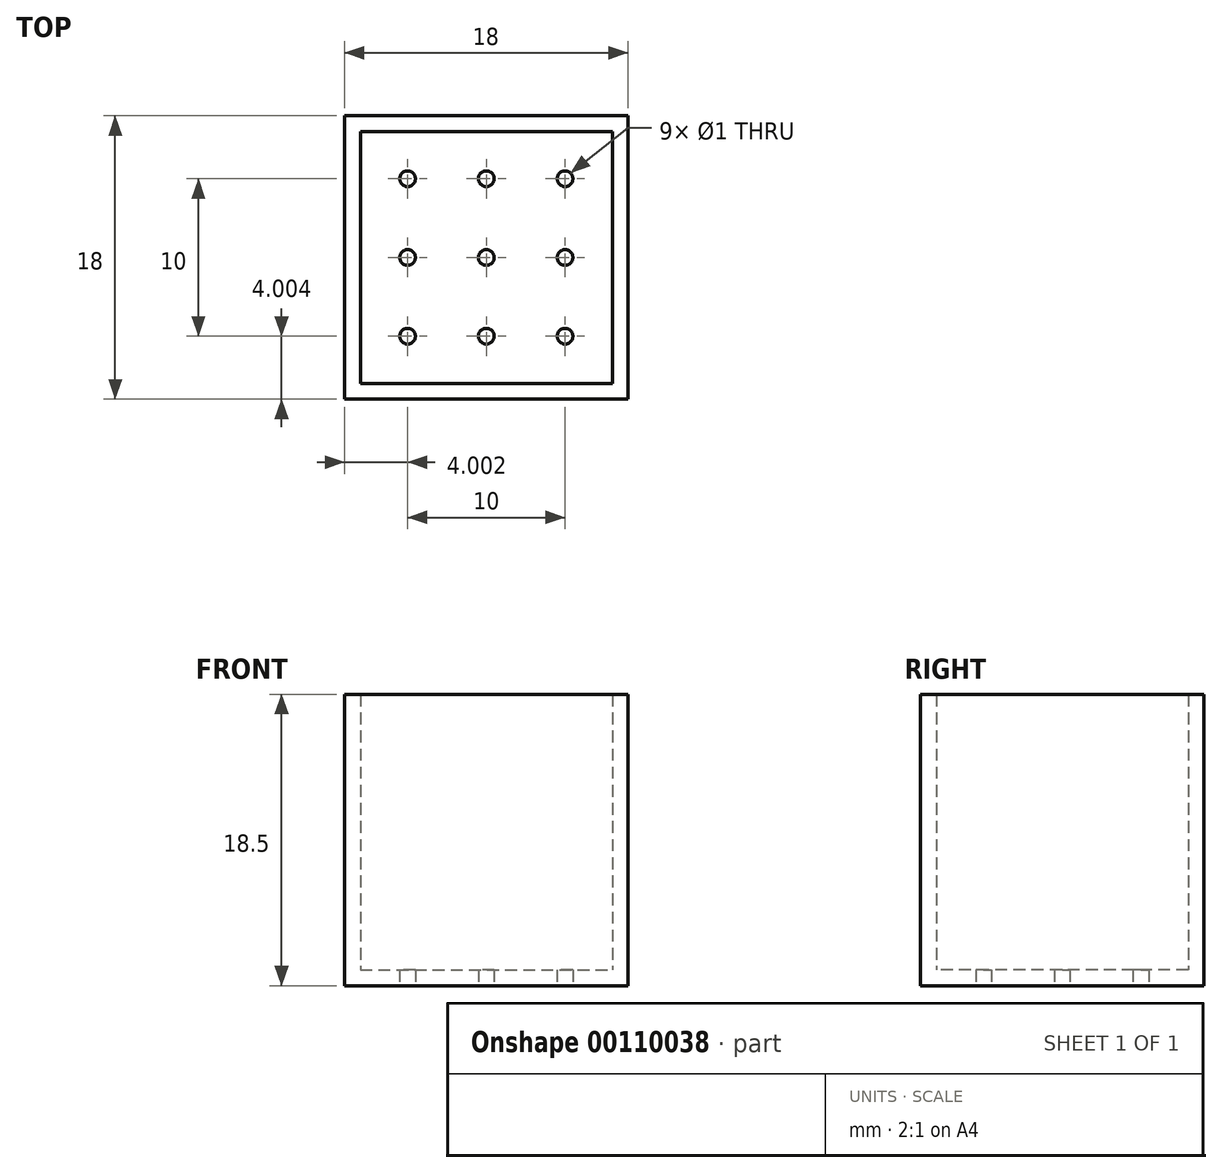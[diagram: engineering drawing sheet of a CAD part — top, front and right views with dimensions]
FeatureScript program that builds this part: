
annotation { "Feature Type Name" : "Feature", "Feature Type Description" : "" }
export const myFeature = defineFeature(function(context is Context, id is Id, definition is map)
    precondition{}
    {
        {
            var Q0;
            Q0=qCreatedBy(makeId("Top.planeOp"),FACE);
            var sketch = newSketch(context, id + "F0", { "sketchPlane" : qUnion([Q0])});
            skLineSegment(sketch, "E0.bottom", {"start": v(-1.53, -8.57) * mm, "end": v(16.47, -8.57) * mm});
            skLineSegment(sketch, "E0.top", {"start": v(-1.53, -26.57) * mm, "end": v(16.47, -26.57) * mm});
            skLineSegment(sketch, "E0.left", {"start": v(-1.53, -8.57) * mm, "end": v(-1.53, -26.57) * mm});
            skLineSegment(sketch, "E0.right", {"start": v(16.47, -8.57) * mm, "end": v(16.47, -26.57) * mm});
            skSolve(sketch);
        }
        {
            var Q0;
            Q0=qSketchRegion(id+"F0",true);
            extrude(context, id + "F1", {"entities" : qUnion([Q0]), "depth" : 18.5 * mm});
        }
        {
            var Q0;
            Q0=makeQuery(id+"F1.opExtrude","CAP_FACE",FACE,{"disambiguationData":[OSD([sQuery(id+"F0.wireOp",EDGE,"E0.bottom"),sQuery(id+"F0.wireOp",EDGE,"E0.top"),sQuery(id+"F0.wireOp",EDGE,"E0.left"),sQuery(id+"F0.wireOp",EDGE,"E0.right")])],"isStart":false});
            shell(context, id + "F2", {"entities" : qUnion([Q0]), "thickness" : 1 * mm});
        }
        {
            var Q0;
            Q0=makeQuery(id+"F1.opExtrude","CAP_FACE",FACE,{"disambiguationData":[OSD([sQuery(id+"F0.wireOp",EDGE,"E0.bottom"),sQuery(id+"F0.wireOp",EDGE,"E0.top"),sQuery(id+"F0.wireOp",EDGE,"E0.left"),sQuery(id+"F0.wireOp",EDGE,"E0.right")])],"isStart":true});
            var sketch = newSketch(context, id + "F3", { "sketchPlane" : qUnion([Q0])});
            skPoint(sketch, "E1", {"position": v(12.47, 22.57) * mm});
            skPoint(sketch, "E2.0.1.0", {"position": v(12.47, 17.57) * mm});
            skPoint(sketch, "E2.0.2.0", {"position": v(12.47, 12.57) * mm});
            skPoint(sketch, "E2.1.0.0", {"position": v(7.47, 22.57) * mm});
            skPoint(sketch, "E2.1.1.0", {"position": v(7.47, 17.57) * mm});
            skPoint(sketch, "E2.1.2.0", {"position": v(7.47, 12.57) * mm});
            skPoint(sketch, "E2.2.0.0", {"position": v(2.47, 22.57) * mm});
            skPoint(sketch, "E2.2.1.0", {"position": v(2.47, 17.57) * mm});
            skPoint(sketch, "E2.2.2.0", {"position": v(2.47, 12.57) * mm});
            skLineSegment(sketch, "E2.direction1", {"start": v(12.47, 22.57) * mm, "end": v(7.47, 22.57) * mm, "construction": true});
            skLineSegment(sketch, "E2.direction2", {"start": v(12.47, 22.57) * mm, "end": v(12.47, 17.57) * mm, "construction": true});
            skSolve(sketch);
        }
        {
            var Q0;
            Q0=sQuery(id+"F3.wireOp",VERTEX,"E1");
            var Q1;
            Q1=sQuery(id+"F3.wireOp",VERTEX,"E2.1.1.0");
            var Q2;
            Q2=sQuery(id+"F3.wireOp",VERTEX,"E2.2.2.0");
            var Q3;
            Q3=sQuery(id+"F3.wireOp",VERTEX,"E2.1.2.0");
            var Q4;
            Q4=sQuery(id+"F3.wireOp",VERTEX,"E2.0.2.0");
            var Q5;
            Q5=sQuery(id+"F3.wireOp",VERTEX,"E2.0.1.0");
            var Q6;
            Q6=sQuery(id+"F3.wireOp",VERTEX,"E2.2.1.0");
            var Q7;
            Q7=sQuery(id+"F3.wireOp",VERTEX,"E2.2.0.0");
            var Q8;
            Q8=sQuery(id+"F3.wireOp",VERTEX,"E2.1.0.0");
            var Q9;
            Q9=makeQuery(id+"F1.opExtrude","SWEPT_BODY",BODY,{"disambiguationData":[OSD([sQuery(id+"F0.wireOp",EDGE,"E0.bottom"),sQuery(id+"F0.wireOp",EDGE,"E0.top"),sQuery(id+"F0.wireOp",EDGE,"E0.left"),sQuery(id+"F0.wireOp",EDGE,"E0.right")])]});
            hole(context, id + "F4", {"style" : HoleStyle.SIMPLE, "endStyle" : HoleEndStyle.THROUGH, "holeDiameter" : 1 * mm, "locations" : qUnion([Q0, Q1, Q2, Q3, Q4, Q5, Q6, Q7, Q8]), "scope" : qUnion([Q9]), "isTappedThrough" : true});
        }
    });
